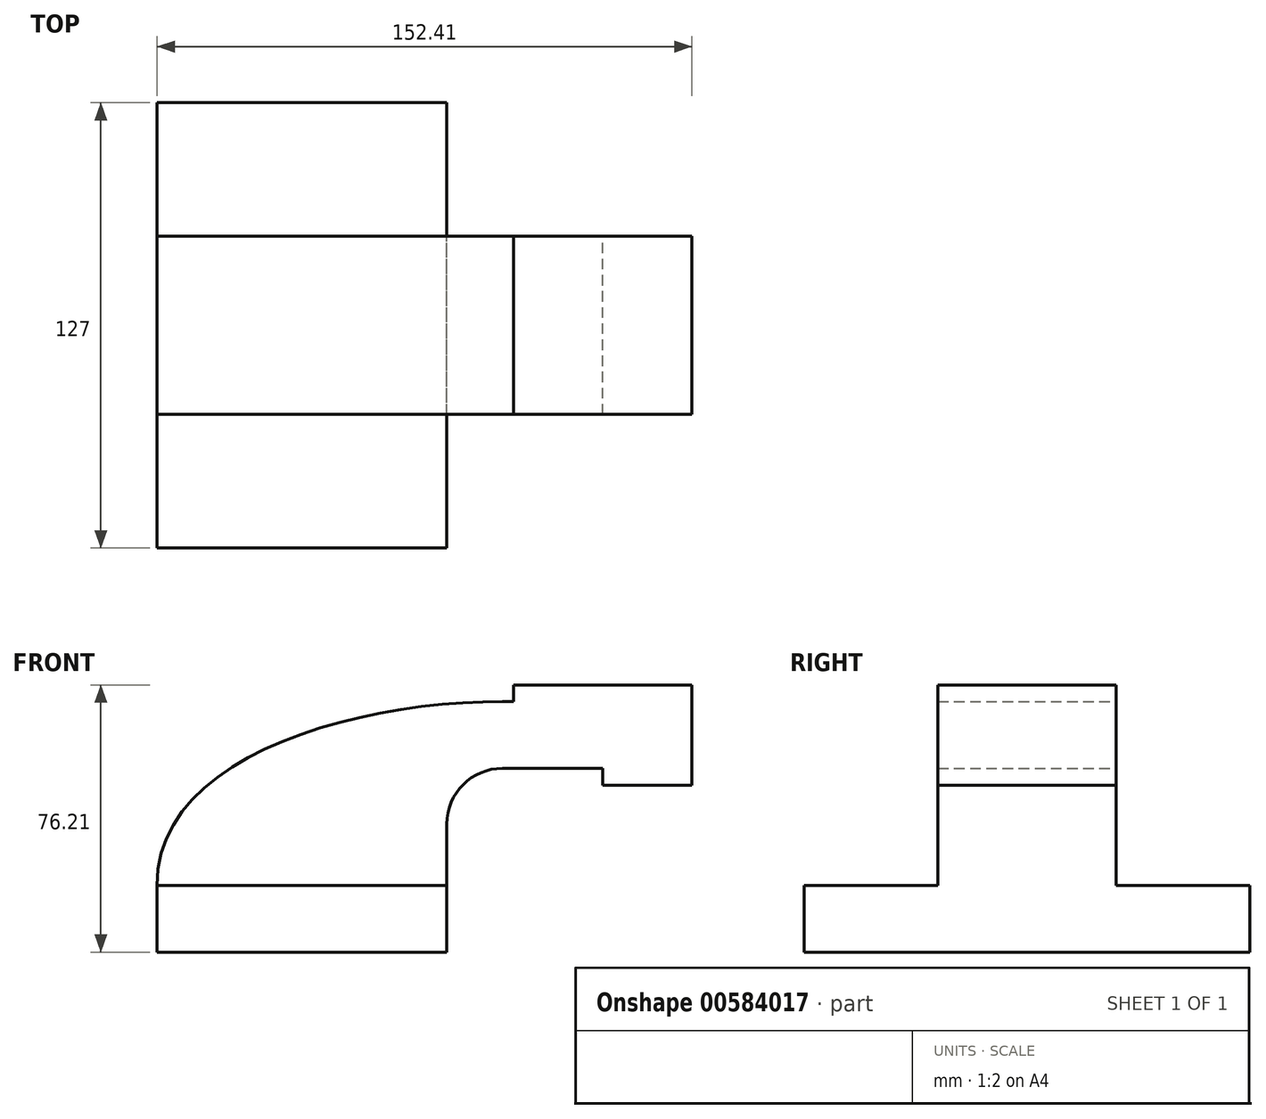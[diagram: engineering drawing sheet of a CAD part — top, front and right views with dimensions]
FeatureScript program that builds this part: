
annotation { "Feature Type Name" : "Feature", "Feature Type Description" : "" }
export const myFeature = defineFeature(function(context is Context, id is Id, definition is map)
    precondition{}
    {
        {
            var Q0;
            Q0=qCreatedBy(makeId("Front.planeOp"),FACE);
            var sketch = newSketch(context, id + "F0", { "sketchPlane" : qUnion([Q0])});
            skLineSegment(sketch, "E0.bottom", {"start": v(41.28, -9.53) * mm, "end": v(-41.27, -9.53) * mm});
            skLineSegment(sketch, "E0.top", {"start": v(41.28, 9.53) * mm, "end": v(-41.28, 9.52) * mm});
            skLineSegment(sketch, "E0.left", {"start": v(41.27, -9.52) * mm, "end": v(41.27, 9.53) * mm});
            skLineSegment(sketch, "E0.right", {"start": v(-41.28, -9.53) * mm, "end": v(-41.28, 9.52) * mm});
            skPoint(sketch, "E0.middle", {"position": v(0, 0) * mm});
            skLineSegment(sketch, "E1.bottom", {"start": v(60.33, 38.1) * mm, "end": v(111.13, 38.1) * mm});
            skLineSegment(sketch, "E1.top", {"start": v(60.33, 66.68) * mm, "end": v(111.13, 66.68) * mm});
            skLineSegment(sketch, "E1.left", {"start": v(60.33, 38.1) * mm, "end": v(60.33, 66.68) * mm});
            skLineSegment(sketch, "E1.right", {"start": v(111.13, 38.1) * mm, "end": v(111.13, 66.68) * mm});
            skLineSegment(sketch, "E2", {"start": v(41.27, 9.53) * mm, "end": v(41.27, 27) * mm});
            skArc(sketch, "E3", {"start": v(41.28, 27) * mm, "mid": v(45.92, 38.23) * mm, "end": v(57.15, 42.88) * mm});
            skLineSegment(sketch, "E4", {"start": v(57.15, 42.88) * mm, "end": v(85.73, 42.88) * mm});
            skLineSegment(sketch, "E5.0", {"start": v(57.15, 61.93) * mm, "end": v(85.76, 61.93) * mm});
            skArc(sketch, "E5.1", {"start": v(22.23, 27) * mm, "mid": v(32.45, 51.7) * mm, "end": v(57.15, 61.93) * mm});
            skLineSegment(sketch, "E5.2", {"start": v(22.23, 9.53) * mm, "end": v(22.23, 27) * mm});
            skPoint(sketch, "E6", {"position": v(85.73, 38.1) * mm});
            skLineSegment(sketch, "E7", {"start": v(85.73, 38.1) * mm, "end": v(85.73, 66.68) * mm});
            skFitSpline(sketch, "E8", {"points": [v(-41.28, 9.52) * mm, v(57.15, 61.93) * mm], "startDerivative": vector(-0.82, 109.86) * mm, "endDerivative": vector(127.9, 0) * mm});
            skSolve(sketch);
        }
        {
            var Q0;
            Q0=makeQuery(id+"F0.imprint","IMPRINT",FACE,{"disambiguationData":[TD([[makeQuery(id+"F0.imprint","IMPRINT",EDGE,{"derivedFrom":sQuery(id+"F0.wireOp",EDGE,"E0.bottom")}),-1.0]])]});
            extrude(context, id + "F1", {"entities" : qUnion([Q0]), "endBound" : BoundingType.SYMMETRIC, "depth" : 127 * mm, "offsetDistance" : 25.4 * mm});
        }
        {
            var Q0;
            Q0=makeQuery(id+"F0.imprint","IMPRINT",FACE,{"disambiguationData":[TD([[makeQuery(id+"F0.imprint","IMPRINT",EDGE,{"derivedFrom":sQuery(id+"F0.wireOp",EDGE,"E0.top")}),-1.0]])]});
            extrude(context, id + "F2", {"entities" : qUnion([Q0]), "operationType" : NewBodyOperationType.ADD, "endBound" : BoundingType.SYMMETRIC, "depth" : 50.8 * mm, "offsetDistance" : 25.4 * mm});
        }
        {
            var Q0;
            {var subQ0=sQuery(id+"F0.wireOp",EDGE,"E4");var subQ1=sQuery(id+"F0.wireOp",EDGE,"E1.left");var subQ2=makeQuery(id+"F0.imprint","INTERSECT",VERTEX,{"derivedFrom":[subQ1,subQ0]});Q0=makeQuery(id+"F0.imprint","IMPRINT",FACE,{"disambiguationData":[TD([[makeQuery(id+"F0.imprint","IMPRINT",EDGE,{"disambiguationData":[TD([[subQ2,-1.0]])],"derivedFrom":subQ1}),-1.0]])]});}
            extrude(context, id + "F3", {"entities" : qUnion([Q0]), "operationType" : NewBodyOperationType.ADD, "endBound" : BoundingType.SYMMETRIC, "depth" : 50.8 * mm, "offsetDistance" : 25.4 * mm});
        }
        {
            var Q0;
            {var subQ4=sQuery(id+"F0.wireOp",EDGE,"E1.right");Q0=makeQuery(id+"F0.imprint","IMPRINT",FACE,{"disambiguationData":[TD([[makeQuery(id+"F0.imprint","IMPRINT",EDGE,{"derivedFrom":subQ4}),1.0]])]});}
            extrude(context, id + "F4", {"entities" : qUnion([Q0]), "operationType" : NewBodyOperationType.ADD, "endBound" : BoundingType.SYMMETRIC, "depth" : 50.8 * mm, "offsetDistance" : 25.4 * mm});
        }
        {
            var Q0;
            {var subQ0=sQuery(id+"F0.wireOp",EDGE,"E1.left");var subQ1=sQuery(id+"F0.wireOp",EDGE,"E1.top");var subQ2=makeQuery(id+"F0.imprint","INTERSECT",VERTEX,{"derivedFrom":[subQ1,subQ0]});Q0=makeQuery(id+"F0.imprint","IMPRINT",FACE,{"disambiguationData":[TD([[makeQuery(id+"F0.imprint","IMPRINT",EDGE,{"disambiguationData":[TD([[subQ2,-1.0]])],"derivedFrom":subQ1}),-1.0]])]});}
            extrude(context, id + "F5", {"entities" : qUnion([Q0]), "operationType" : NewBodyOperationType.ADD, "endBound" : BoundingType.SYMMETRIC, "depth" : 50.8 * mm, "offsetDistance" : 25.4 * mm});
        }
    });
